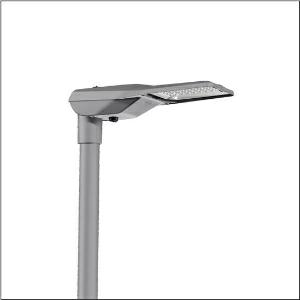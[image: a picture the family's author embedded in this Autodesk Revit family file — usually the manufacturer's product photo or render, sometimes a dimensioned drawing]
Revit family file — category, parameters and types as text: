
# Revit family: streetlight_sl_21_iq_mini___st1_5a_5xe2p31y08gb_2fd1
name_source: partatom
category: Lighting Fixtures
units: mm (PartAtom-declared; Revit-internal decimal feet)

## family parameters
Cut with Voids When Loaded = No
Host = Face
Light Source = No
Part Type = Normal
Room Calculation Point = No
Round Connector Dimension = Use Diameter
Shared = No

## types (1)
- --- (1 x LED, 5880 lm, 39.8 W, 3000K)
    Apparent Load = 40 VA
    CIE Flux Codes = 22 53 95 100 100
    Color Rendering = 70
    Color Temperature = 3000K
    Default Elevation = 1800 mm
    Description = Streetlight SL 21 iQ mini, mast luminaire, primary light control with lens, of PMMA, primary optical cover: cover, of toughened safety glass, transparent, light distribution: ST1.5a, light emission: direct distribution, primary light characteristic: asymmetric, installation type: post-top, side-entry, LED, High Power LED, rated luminous flux: 5.880lm, luminous efficacy: 148lm/W, light colour: 730, colour temperature: 3000K, control: presetting dimming logarithmic, Street-Remote, Auto-Match, Temp-Guard, Lumen-Switch, Night-Set, Smart-Wire, Light-Fading, Desk-Remote (wireless, voltage-free reading and setting of iQ features in the workshop via application-optimized NFC function/RFID function), optimised constant luminous flux control (CLO 2.0), mains connection: 220..240V, AC, 50/60Hz, start of lifetime: 40W, end of service life: 41W, reduction: 18W, luminaire housing, of diecast aluminium, powder-coated, Siteco® metallic grey (DB 702S), corrosivity category C5 mid according to DIN EN ISO 12944, please order mast flange separately, inclination adjustable: 0°, 5°, 10°, 15°, sealing non-destructively replaceable, multi-level sealing system, length: 628mm, width: 235mm, height: 110mm, mast flange for spigot size: 42mm (side-entry): 5XC10008XM4, 60/48mm (side-entry/post-top): 5XC10108XM2, 76/60mm (side-entry/post-top): 5XC10108XM1, Smart Interface below and above, protection rating (complete): IP66, insulation class (complete): insulation class II (safety insulation), certification: CE, ENEC, ENEC+, VDE, impact resistance: IK09, permissible operating ambient temperature for outdoor applications: -40..+50°C, standard-compliant lighting for roads and squares, packaging unit: 1 piece

Light Distribution: ST1.5a
    Height = 110 mm
    Lamp = 1 x LED
    Lamp Light Flux = 5880 lm
    Lamp Power = 39.8 W
    Lamp count = 1
    Length = 625 mm
    Luminous efficacy = 148 lm/W
    Manufacturer = Siteco
    ModVariant = No
    Model = 5XE2P31Y08GB
    Number of Poles = 1
    OnlyDefault = Yes
    Power Factor = 1
    Product Name = Streetlight SL 21 iQ mini | ST1.5a
    Product group = mast luminaire | pylon top
    ProductGroupID = 6100
    Protection Class = Protection class II
    Protection Degree = IP 66
    RLX_Detail_Level = 1
    RLX_Emergency_Light_Flux = 0 lm
    RLX_Emergency_Type = 0
    RLX_Emergency_Type_DB = No
    RlxData = <blob elided: 96529 chars, md5=89d10425>
    Socket = socket
    Standby Power = 0 W
    System Light Flux = 5880 lm
    System Power = 40 W
    Type Comments = factory setting: luminous flux: 100 % | dim-lin: 254 | 800 mA
    Type Image = l_1003514.jpg
    URL = http://relux.com
    VarID = @adj_060183
    Voltage = 0 V
    Weight = 0.00 kg
    Width = 234 mm

## geometry (parser evidence)
native form markers: Blend x4, Sweep x11
no freeform markers — native parametric forms only
